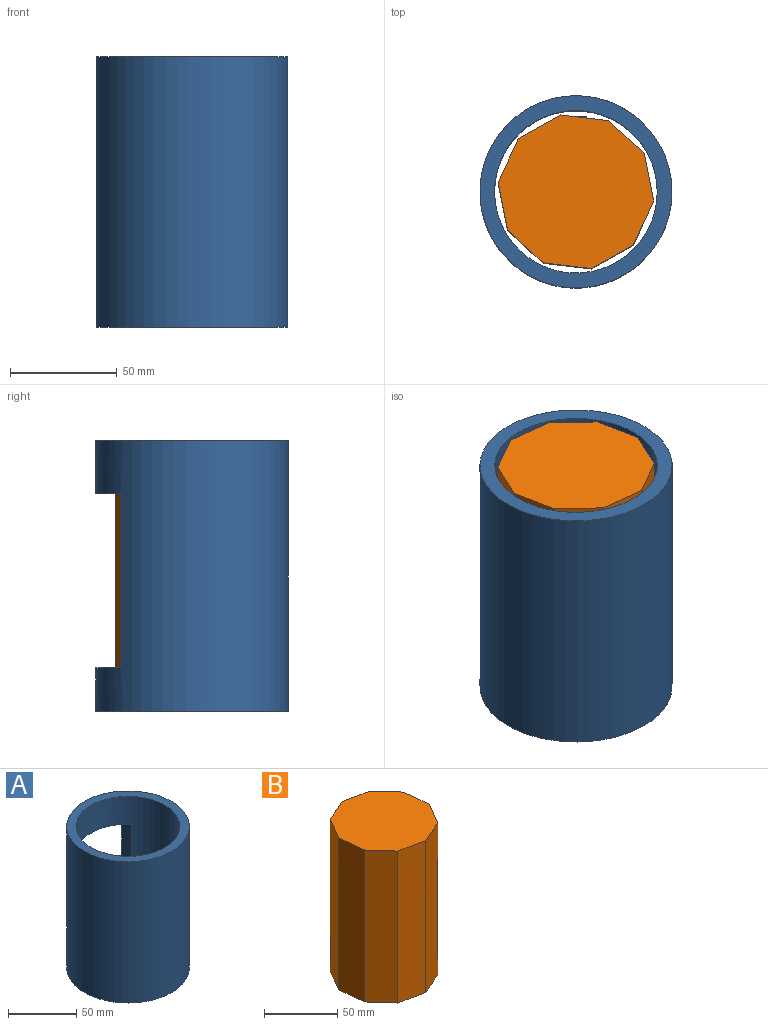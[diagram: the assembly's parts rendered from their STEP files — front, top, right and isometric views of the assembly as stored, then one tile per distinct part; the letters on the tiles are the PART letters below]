
ASSEMBLY  parts=2 mates=1
PART A: 8 faces, bbox 90.1x90.1x127 mm
  f0: cylinder r=45.05mm len=127mm, axis (0,0,-1), area 30716.1mm2, adj f2,f3,f4,f5,f6,f7
  f1: cylinder r=38.1mm len=127mm, axis (0,0,1), area 24911mm2, adj f2,f3,f4,f5,f6,f7
  f2: plane 90.11x90.11mm, normal (0,0,1), area 1816.5mm2, adj f0,f1
  f3: plane 90.11x90.11mm, normal (0,0,-1), area 1816.5mm2, adj f0,f1
  f4: plane 58.81x21.9mm, normal (0,0,-1), area 455.2mm2, adj f0,f1,f5,f7
  f5: plane 81.67x10.23mm, normal (1,0,0), area 835.3mm2, adj f0,f1,f4,f6
  f6: plane 58.81x21.9mm, normal (0,0,1), area 455.2mm2, adj f0,f1,f5,f7
  f7: plane 81.67x9.62mm, normal (-1,0,0), area 786mm2, adj f0,f1,f4,f6
PART B: 21 faces, bbox 71.8x73.1x127 mm
  f0: plane 127x22.18mm, normal (-0.21,-0.98,0), area 2882.3mm2, adj f1,f9,f10,f11
  f1: plane 127x20.77mm, normal (0.4,-0.92,0), area 2882.3mm2, adj f0,f2,f10,f11
  f2: plane 127x19.61mm, normal (0.86,-0.5,0), area 2882.3mm2, adj f1,f3,f10,f11
  f3: plane 127x22.58mm, normal (0.99,0.1,0), area 2882.3mm2, adj f2,f4,f10,f11
  f4: plane 127x16.93mm, normal (0.75,0.67,0), area 2876.9mm2, adj f3,f5,f10,f11,f12,f15,f18
  f5: plane 127x22.18mm, normal (0.21,0.98,0), area 2882.3mm2, adj f4,f6,f10,f11
  f6: plane 127x20.77mm, normal (-0.4,0.92,0), area 2882.3mm2, adj f5,f7,f10,f11
  f7: plane 127x19.61mm, normal (-0.86,0.5,0), area 2882.3mm2, adj f6,f8,f10,f11
  f8: plane 127x22.58mm, normal (-0.99,-0.1,0), area 2882.3mm2, adj f7,f9,f10,f11
  f9: plane 127x16.93mm, normal (-0.75,-0.67,0), area 2882.3mm2, adj f0,f8,f10,f11
  f10: plane 73.07x71.78mm, normal (0,0,1), area 3963.2mm2, adj f0,f1,f2,f3,f4,f5,f6,f7
  f11: plane 73.07x71.78mm, normal (0,0,-1), area 3963.2mm2, adj f0,f1,f2,f3,f4,f5,f6,f7
  f12: cylinder r=0.76mm len=1.53mm, axis (-0.75,-0.67,0), area 1.8mm2, adj f4,f14
  f13: plane 1.02x0.76mm, normal (0.75,0.67,0), area 0.8mm2, adj f14
  f14: torus R=0.51mm, axis (0.75,0.67,0), area 1.7mm2, adj f12,f13
  f15: cylinder r=0.76mm len=1.53mm, axis (-0.75,-0.67,0), area 1.8mm2, adj f4,f17
  f16: plane 1.02x0.76mm, normal (0.75,0.67,0), area 0.8mm2, adj f17
  f17: torus R=0.51mm, axis (0.75,0.67,0), area 1.7mm2, adj f15,f16
  f18: cylinder r=0.76mm len=1.53mm, axis (-0.75,-0.67,0), area 1.8mm2, adj f4,f20
  f19: plane 1.02x0.76mm, normal (0.75,0.67,0), area 0.8mm2, adj f20
  f20: torus R=0.51mm, axis (0.75,0.67,0), area 1.7mm2, adj f18,f19
PLACE A t=(6.62,-16.7,-26.29)mm
PLACE B rot(axis=(-0.46,-0.89,0),180deg) t=(6.62,-16.7,100.71)mm
MATE revolute B.f10 <-> A.f1  axis (0,0,-1) through (6.62,-16.7,-26.29)mm
